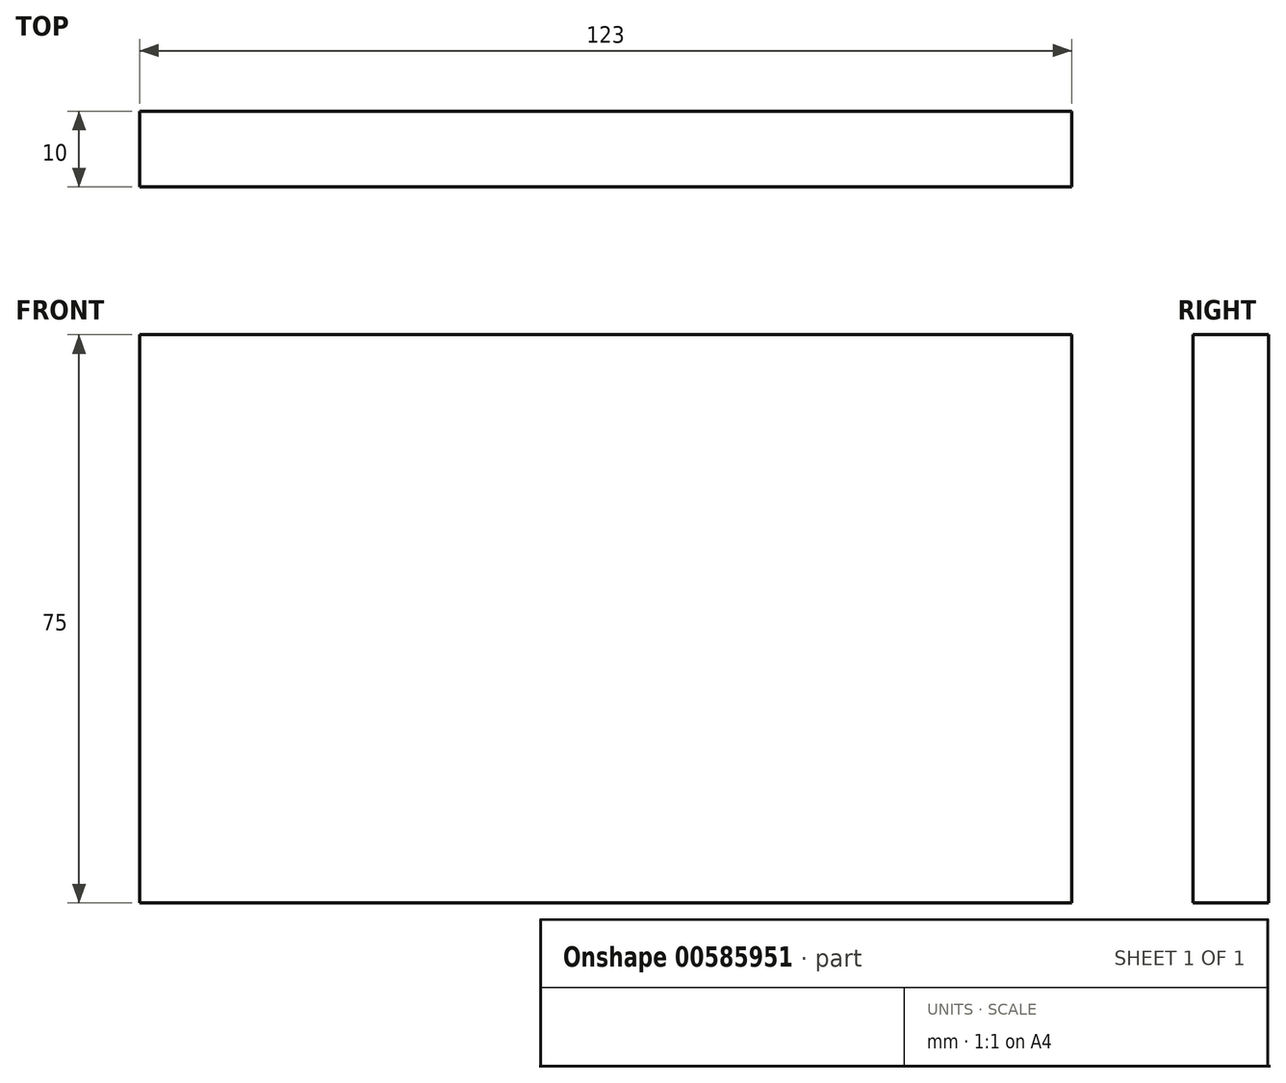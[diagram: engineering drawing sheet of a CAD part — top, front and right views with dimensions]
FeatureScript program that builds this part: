
annotation { "Feature Type Name" : "Feature", "Feature Type Description" : "" }
export const myFeature = defineFeature(function(context is Context, id is Id, definition is map)
    precondition{}
    {
        {
            var Q0;
            Q0=qCreatedBy(makeId("Top.planeOp"),FACE);
            var sketch = newSketch(context, id + "F0", { "sketchPlane" : qUnion([Q0])});
            skLineSegment(sketch, "E0.bottom", {"start": v(61.5, 5) * mm, "end": v(-61.5, 5) * mm});
            skLineSegment(sketch, "E0.top", {"start": v(61.5, -5) * mm, "end": v(-61.5, -5) * mm});
            skLineSegment(sketch, "E0.left", {"start": v(61.5, 5) * mm, "end": v(61.5, -5) * mm});
            skLineSegment(sketch, "E0.right", {"start": v(-61.5, 5) * mm, "end": v(-61.5, -5) * mm});
            skPoint(sketch, "E0.middle", {"position": v(0, 0) * mm});
            skSolve(sketch);
        }
        {
            var Q0;
            Q0=makeQuery(id+"F0.imprint","IMPRINT",FACE,{"disambiguationData":[TD([[makeQuery(id+"F0.imprint","IMPRINT",EDGE,{"derivedFrom":sQuery(id+"F0.wireOp",EDGE,"E0.bottom")}),1.0]])]});
            extrude(context, id + "F1", {"entities" : qUnion([Q0]), "depth" : 75 * mm, "offsetDistance" : 25 * mm});
        }
    });
